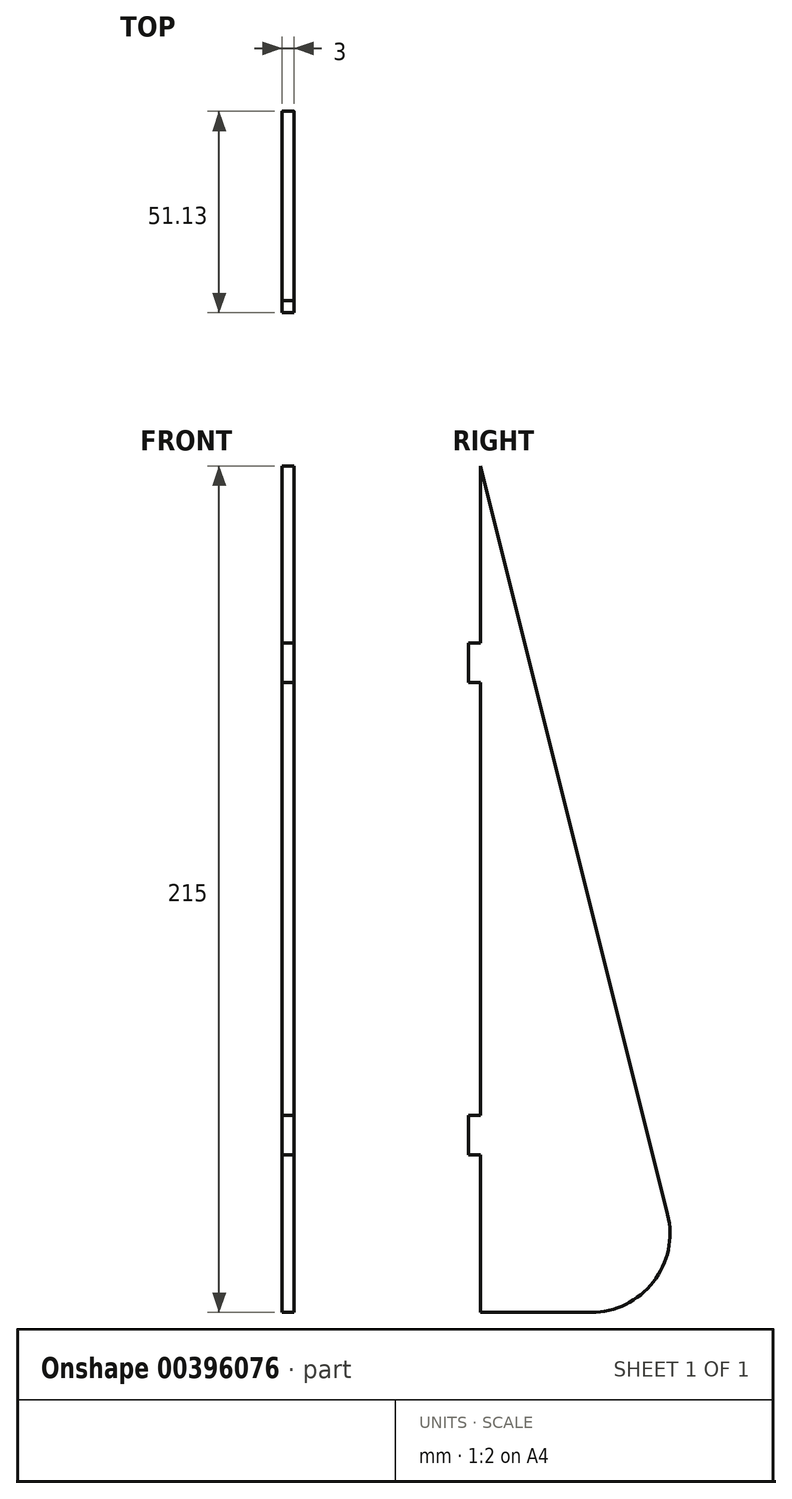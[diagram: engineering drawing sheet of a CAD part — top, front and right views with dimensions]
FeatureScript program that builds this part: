
annotation { "Feature Type Name" : "Feature", "Feature Type Description" : "" }
export const myFeature = defineFeature(function(context is Context, id is Id, definition is map)
    precondition{}
    {
        {
            var Q0;
            Q0=qCreatedBy(makeId("Right.planeOp"),FACE);
            var sketch = newSketch(context, id + "F0", { "sketchPlane" : qUnion([Q0])});
            skLineSegment(sketch, "E0", {"start": v(0, 220) * mm, "end": v(47.54, 29.85) * mm});
            skLineSegment(sketch, "E1", {"start": v(0, 5) * mm, "end": v(0, 220) * mm});
            skLineSegment(sketch, "E2", {"start": v(0, 175) * mm, "end": v(-3, 175) * mm});
            skLineSegment(sketch, "E3", {"start": v(-3, 175) * mm, "end": v(-3, 165) * mm});
            skLineSegment(sketch, "E4", {"start": v(-3, 165) * mm, "end": v(0, 165) * mm});
            skLineSegment(sketch, "E5", {"start": v(0, 55) * mm, "end": v(-3, 55) * mm});
            skLineSegment(sketch, "E6", {"start": v(-3, 55) * mm, "end": v(-3, 45) * mm});
            skLineSegment(sketch, "E7", {"start": v(-3, 45) * mm, "end": v(0, 45) * mm});
            skPoint(sketch, "E8.visualSharp", {"position": v(55, 0) * mm});
            skPoint(sketch, "E9.end.orphan", {"position": v(0, 0) * mm});
            skLineSegment(sketch, "E10", {"start": v(0, 5) * mm, "end": v(28.13, 5) * mm});
            skPoint(sketch, "E11.visualSharp", {"position": v(53.75, 5) * mm});
            skArc(sketch, "E11.filletArc", {"start": v(28.13, 5) * mm, "mid": v(43.9, 12.7) * mm, "end": v(47.54, 29.85) * mm});
            skSolve(sketch);
        }
        {
            var Q0;
            Q0 = qSketchRegion(id + "F0", true);
            extrude(context, id + "F1", {"entities" : qUnion([Q0]), "depth" : 3 * mm});
        }
    });
